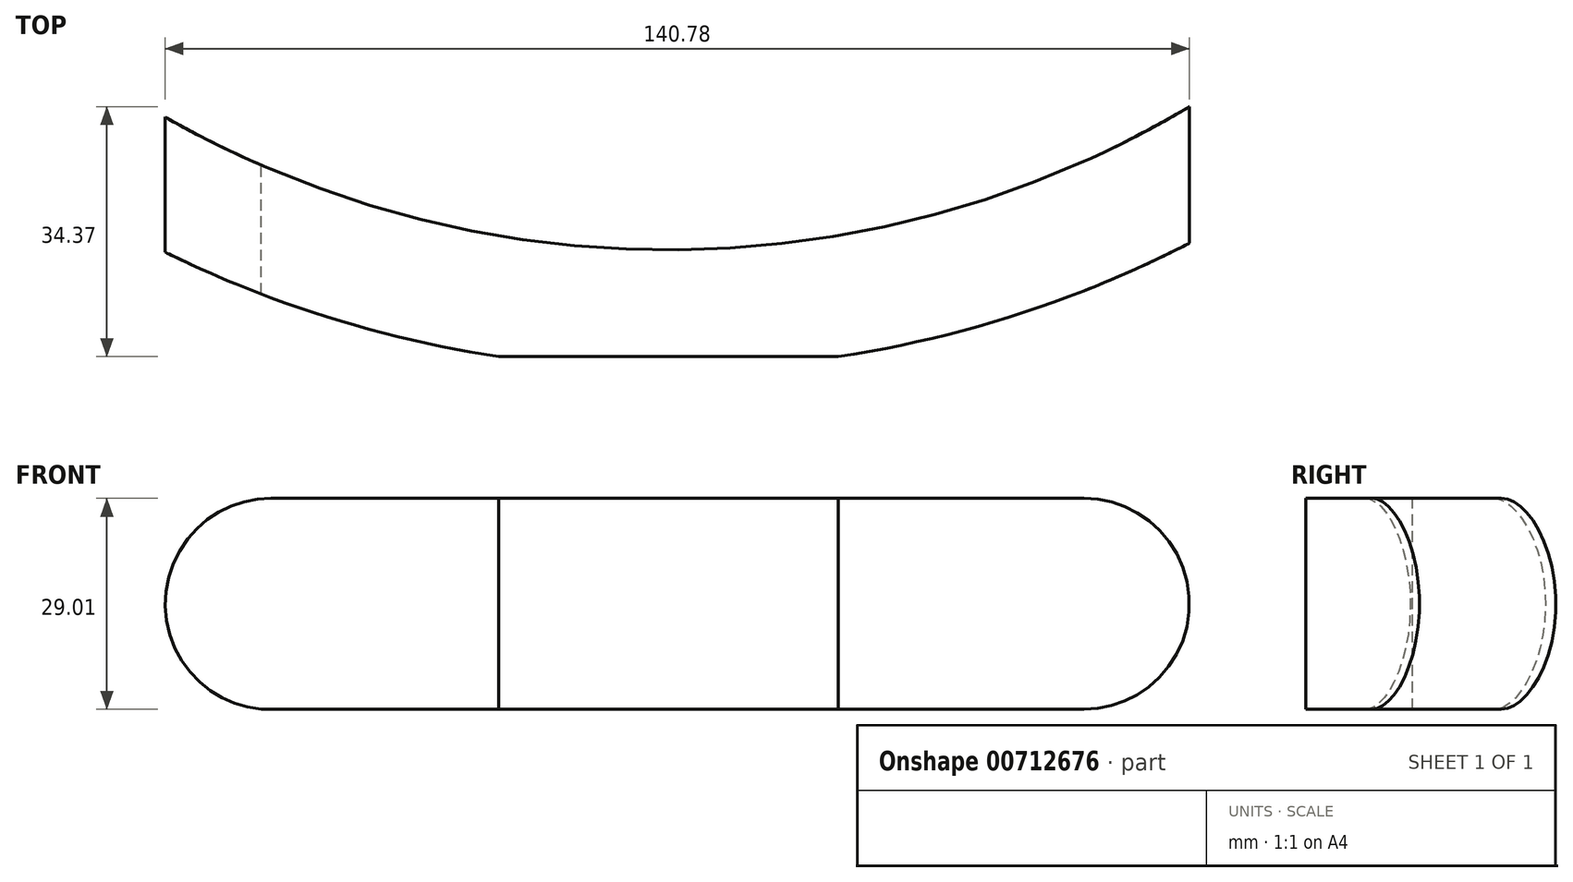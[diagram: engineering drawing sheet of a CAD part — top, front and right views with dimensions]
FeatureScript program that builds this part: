
annotation { "Feature Type Name" : "Feature", "Feature Type Description" : "" }
export const myFeature = defineFeature(function(context is Context, id is Id, definition is map)
    precondition{}
    {
        {
            var Q0;
            Q0=qCreatedBy(makeId("Front.planeOp"),FACE);
            var sketch = newSketch(context, id + "F0", { "sketchPlane" : qUnion([Q0])});
            skLineSegment(sketch, "E0", {"start": v(-54.62, 0) * mm, "end": v(57.11, 0) * mm});
            skArc(sketch, "E1", {"start": v(-54.62, 0) * mm, "mid": v(-69.14, -13.86) * mm, "end": v(-55.98, -29) * mm});
            skLineSegment(sketch, "E2", {"start": v(-55.98, -29) * mm, "end": v(57.11, -29) * mm});
            skArc(sketch, "E3", {"start": v(57.11, 0) * mm, "mid": v(71.62, -14.5) * mm, "end": v(57.11, -29) * mm});
            skSolve(sketch);
        }
        {
            var Q0;
            Q0=makeQuery(id+"F0.imprint","IMPRINT",FACE,{"disambiguationData":[TD([[makeQuery(id+"F0.imprint","IMPRINT",EDGE,{"derivedFrom":sQuery(id+"F0.wireOp",EDGE,"E0")}),-1.0]])]});
            extrude(context, id + "F1", {"entities" : qUnion([Q0]), "depth" : 35 * mm, "offsetDistance" : 25 * mm});
        }
        {
            var Q0;
            Q0=qCreatedBy(makeId("Top.planeOp"),FACE);
            var sketch = newSketch(context, id + "F2", { "sketchPlane" : qUnion([Q0])});
            skArc(sketch, "E4", {"start": v(-105.22, 27.32) * mm, "mid": v(-1.66, -20.32) * mm, "end": v(103, 24.84) * mm});
            skLineSegment(sketch, "E5", {"start": v(0, 111.38) * mm, "end": v(0, -93.96) * mm, "construction": true});
            skLineSegment(sketch, "E6", {"start": v(-105.22, 27.32) * mm, "end": v(103, 24.84) * mm});
            skArc(sketch, "E7.0", {"start": v(-117.56, 16.49) * mm, "mid": v(-1.86, -36.74) * mm, "end": v(115.08, 13.72) * mm});
            skLineSegment(sketch, "E8", {"start": v(-117.56, 16.49) * mm, "end": v(-117.56, -55.87) * mm});
            skLineSegment(sketch, "E9", {"start": v(-117.56, -55.87) * mm, "end": v(118.52, -63.76) * mm});
            skLineSegment(sketch, "E10", {"start": v(118.52, -63.76) * mm, "end": v(115.08, 13.72) * mm});
            skSolve(sketch);
        }
        {
            var Q0;
            Q0=makeQuery(id+"F2.imprint","IMPRINT",FACE,{"disambiguationData":[TD([[makeQuery(id+"F2.imprint","IMPRINT",EDGE,{"derivedFrom":sQuery(id+"F2.wireOp",EDGE,"E4")}),1.0]])]});
            extrude(context, id + "F3", {"entities" : qUnion([Q0]), "operationType" : NewBodyOperationType.REMOVE, "endBound" : BoundingType.THROUGH_ALL, "oppositeDirection" : true, "depth" : 25 * mm, "offsetDistance" : 25 * mm});
        }
        {
            var Q0;
            Q0=makeQuery(id+"F2.imprint","IMPRINT",FACE,{"disambiguationData":[TD([[makeQuery(id+"F2.imprint","IMPRINT",EDGE,{"derivedFrom":sQuery(id+"F2.wireOp",EDGE,"E7.0")}),-1.0]])]});
            extrude(context, id + "F4", {"entities" : qUnion([Q0]), "operationType" : NewBodyOperationType.REMOVE, "endBound" : BoundingType.THROUGH_ALL, "oppositeDirection" : true, "depth" : 25 * mm, "offsetDistance" : 25 * mm});
        }
    });
